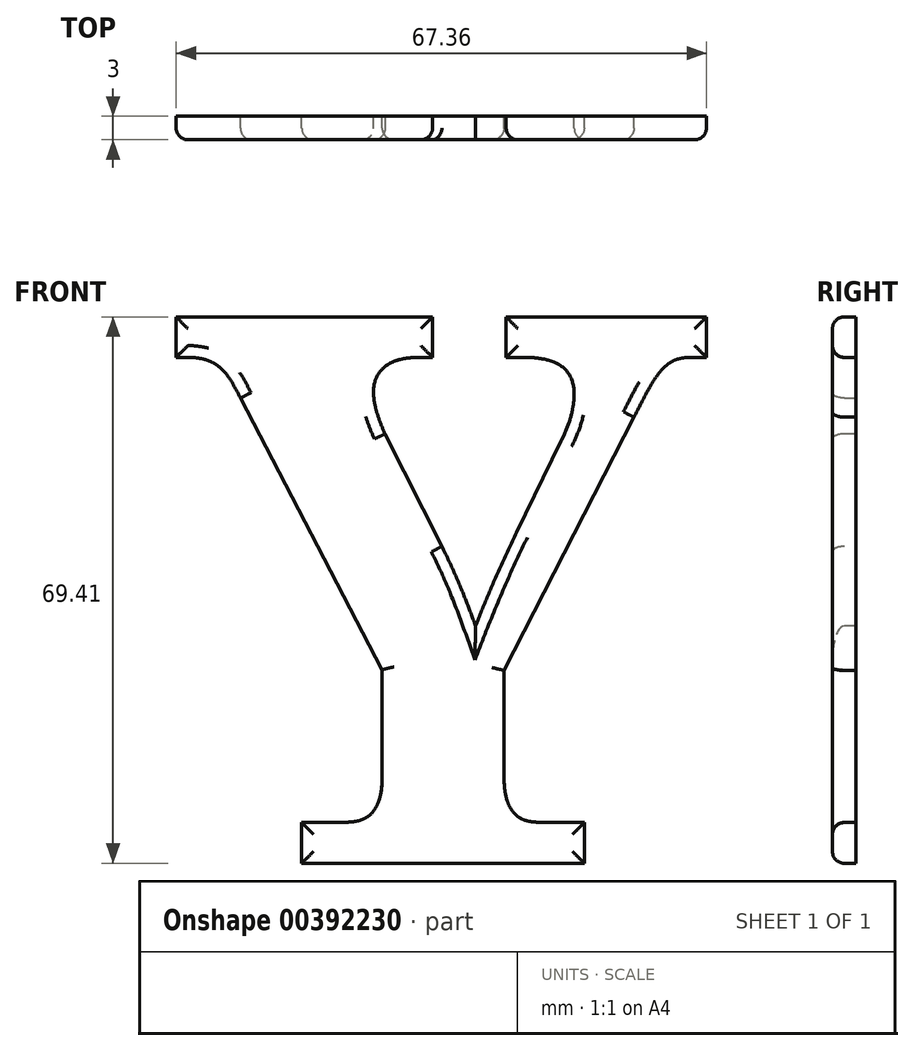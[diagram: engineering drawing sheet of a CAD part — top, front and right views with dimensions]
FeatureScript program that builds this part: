
annotation { "Feature Type Name" : "Feature", "Feature Type Description" : "" }
export const myFeature = defineFeature(function(context is Context, id is Id, definition is map)
    precondition{}
    {
        {
            var Q0;
            Q0=qCreatedBy(makeId("Front.planeOp"),FACE);
            var sketch = newSketch(context, id + "F0", { "sketchPlane" : qUnion([Q0])});
            skText(sketch, "E0", { "text": "Y", "fontName": "NotoSerif-Bold.ttf"});
            const initialGuessF0  = {"E0": [0, 0, 1, 0, 0.07]};
            skSetInitialGuess(sketch, initialGuessF0);
            skSolve(sketch);
        }
        {
            var Q0;
            Q0 = qSketchRegion(id + "F0", true);
            extrude(context, id + "F1", {"entities" : qUnion([Q0]), "depth" : 3 * mm});
        }
        {
            var Q0;
            Q0=makeQuery(id+"F1.opExtrude","CAP_FACE",FACE,{"disambiguationData":[OSD([sQuery(id+"F0.wireOp",EDGE,"E0.sketch_text.stroke-0"),sQuery(id+"F0.wireOp",EDGE,"E0.sketch_text.stroke-1"),sQuery(id+"F0.wireOp",EDGE,"E0.sketch_text.stroke-2"),sQuery(id+"F0.wireOp",EDGE,"E0.sketch_text.stroke-3"),sQuery(id+"F0.wireOp",EDGE,"E0.sketch_text.stroke-4"),sQuery(id+"F0.wireOp",EDGE,"E0.sketch_text.stroke-5"),sQuery(id+"F0.wireOp",EDGE,"E0.sketch_text.stroke-6"),sQuery(id+"F0.wireOp",EDGE,"E0.sketch_text.stroke-7"),sQuery(id+"F0.wireOp",EDGE,"E0.sketch_text.stroke-8"),sQuery(id+"F0.wireOp",EDGE,"E0.sketch_text.stroke-9"),sQuery(id+"F0.wireOp",EDGE,"E0.sketch_text.stroke-10"),sQuery(id+"F0.wireOp",EDGE,"E0.sketch_text.stroke-11"),sQuery(id+"F0.wireOp",EDGE,"E0.sketch_text.stroke-12"),sQuery(id+"F0.wireOp",EDGE,"E0.sketch_text.stroke-13"),sQuery(id+"F0.wireOp",EDGE,"E0.sketch_text.stroke-14"),sQuery(id+"F0.wireOp",EDGE,"E0.sketch_text.stroke-15"),sQuery(id+"F0.wireOp",EDGE,"E0.sketch_text.stroke-16"),sQuery(id+"F0.wireOp",EDGE,"E0.sketch_text.stroke-17"),sQuery(id+"F0.wireOp",EDGE,"E0.sketch_text.stroke-18"),sQuery(id+"F0.wireOp",EDGE,"E0.sketch_text.stroke-19"),sQuery(id+"F0.wireOp",EDGE,"E0.sketch_text.stroke-20"),sQuery(id+"F0.wireOp",EDGE,"E0.sketch_text.stroke-21"),sQuery(id+"F0.wireOp",EDGE,"E0.sketch_text.stroke-22"),sQuery(id+"F0.wireOp",EDGE,"E0.sketch_text.stroke-23"),sQuery(id+"F0.wireOp",EDGE,"E0.sketch_text.stroke-24"),sQuery(id+"F0.wireOp",EDGE,"E0.sketch_text.stroke-25"),sQuery(id+"F0.wireOp",EDGE,"E0.sketch_text.stroke-26"),sQuery(id+"F0.wireOp",EDGE,"E0.sketch_text.stroke-27"),sQuery(id+"F0.wireOp",EDGE,"E0.sketch_text.stroke-28"),sQuery(id+"F0.wireOp",EDGE,"E0.sketch_text.stroke-29"),sQuery(id+"F0.wireOp",EDGE,"E0.sketch_text.stroke-30"),sQuery(id+"F0.wireOp",EDGE,"E0.sketch_text.stroke-31"),sQuery(id+"F0.wireOp",EDGE,"E0.sketch_text.stroke-32"),sQuery(id+"F0.wireOp",EDGE,"E0.sketch_text.stroke-33"),sQuery(id+"F0.wireOp",EDGE,"E0.sketch_text.stroke-34"),sQuery(id+"F0.wireOp",EDGE,"E0.sketch_text.stroke-35"),sQuery(id+"F0.wireOp",EDGE,"E0.sketch_text.stroke-36"),sQuery(id+"F0.wireOp",EDGE,"E0.sketch_text.stroke-37"),sQuery(id+"F0.wireOp",EDGE,"E0.sketch_text.stroke-38"),sQuery(id+"F0.wireOp",EDGE,"E0.sketch_text.stroke-39"),sQuery(id+"F0.wireOp",EDGE,"E0.sketch_text.stroke-40"),sQuery(id+"F0.wireOp",EDGE,"E0.sketch_text.stroke-41"),sQuery(id+"F0.wireOp",EDGE,"E0.sketch_text.stroke-42"),sQuery(id+"F0.wireOp",EDGE,"E0.sketch_text.stroke-43"),sQuery(id+"F0.wireOp",EDGE,"E0.sketch_text.stroke-44"),sQuery(id+"F0.wireOp",EDGE,"E0.sketch_text.stroke-45"),sQuery(id+"F0.wireOp",EDGE,"E0.sketch_text.stroke-46"),sQuery(id+"F0.wireOp",EDGE,"E0.sketch_text.stroke-47"),sQuery(id+"F0.wireOp",EDGE,"E0.sketch_text.stroke-48")])],"isStart":false});
            fillet(context, id + "F2", {"entities" : qUnion([Q0]), "radius" : 1.5 * mm, "tangentPropagation" : true, "allowEdgeOverflow" : false});
        }
    });
